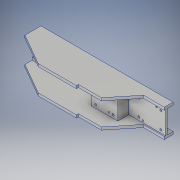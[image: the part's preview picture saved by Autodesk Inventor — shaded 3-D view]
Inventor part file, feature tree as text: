
AUTODESK INVENTOR PART (.ipt)
format: ipt  version: 2017 (Build 210142000, 142)  size: 502,784 bytes
history: native  units: in
note: dims shown in document units (in); Inventor stores cm internally (conversion verified against a paired STEP export)
features: projected_geometry x25, sketch x17, extrude x13, hole x5, reference x4, other x4, chamfer x1
ambient origin geometry x8: Origin, YZ Plane, XZ Plane, XY Plane, X Axis, Y Axis, Z Axis, Center Point
bodies: Solid1 (feature_tree)
feature tree (69):
  extrude  "Extrusion1"  Depth=0.8268in
  extrude  "Extrusion2"  Depth=0.2756in
  extrude  "Extrusion3"  Depth=0.0787in
  extrude  "Extrusion4"  Depth=0.1181in
  extrude  "Extrusion5"  Depth=0.0591in
  hole  "Hole1"  [1 undecoded]
  extrude  "Extrusion6"  Depth=0.0591in
  extrude  "Extrusion7"  Depth=0.7874in
  extrude  "Extrusion8"  Depth=0.2953in TaperAngle=0.0deg
  chamfer  "Chamfer1"  Distance=0.2953in
  hole  "Hole2"  [1 undecoded]
  extrude  "Extrusion9"  Depth=0.4921in
  hole  "Hole3"  [1 undecoded]
  extrude  "Extrusion10"  Depth=0.0591in
  extrude  "Extrusion11"  Depth=0.0591in
  hole  "Hole4"  [1 undecoded]
  extrude  "Extrusion12"  Depth=0.3543in
  hole  "Hole5"  [1 undecoded]
  extrude  "Extrusion13"  Depth=0.2362in
  sketch  "Sketch1"  dims[d0=0.8268in d1=6.4567in]
  sketch  "Sketch2"  dims[d2=1.1417in d3=0.0in d4=0.2756in]
  projected_geometry  "Projected Loop1"
  sketch  "Sketch3"  dims[d5=0.0394in d6=0.0787in]
  sketch  "Sketch4"  dims[d7=0.5906in d8=0.0in d9=0.1181in d10=0.3543in]
  projected_geometry  "Projected Loop2"
  projected_geometry  "Projected Loop3"
  projected_geometry  "Projected Loop4"
  projected_geometry  "Projected Loop5"
  sketch  "Sketch5"  dims[d11=0.1181in d12=0.0591in]
  projected_geometry  "Projected Loop6"
  projected_geometry  "Projected Loop7"
  projected_geometry  "Projected Loop8"
  projected_geometry  "Projected Loop9"
  projected_geometry  "Projected Loop10"
  sketch  "Sketch7"  dims[d13=0.0591in d14=0.0591in]
  projected_geometry  "Projected Loop11"
  sketch  "Sketch8"  dims[d15=0.0591in d16=0.0591in]
  sketch  "Sketch9"  dims[d17=0.0591in d18=0.7874in]
  projected_geometry  "Projected Loop13"
  sketch  "Sketch10"  dims[d19=2.0276in d20=0.2953in d21=0.0in]
  projected_geometry  "Projected Loop14"
  projected_geometry  "Projected Loop15"
  sketch  "Sketch11"  dims[d22=0.2559in]
  projected_geometry  "Projected Loop16"
  sketch  "Sketch12"  dims[d23=0.2953in]
  projected_geometry  "Projected Loop17"
  sketch  "Sketch13"  dims[d24=0.4331in]
  projected_geometry  "Projected Loop18"
  projected_geometry  "Projected Loop19"
  sketch  "Sketch14"  dims[d25=0.9449in]
  projected_geometry  "Projected Loop20"
  projected_geometry  "Projected Loop21"
  sketch  "Sketch15"  dims[d26=0.0787in]
  reference  "Reference1"
  reference  "Reference2"
  sketch  "Sketch16"  dims[d27=0.0787in]
  projected_geometry  "Projected Loop22"
  sketch  "Sketch17"  dims[d28=0.8705in d29=0.2953in d30=0.0in]
  reference  "Reference3"
  reference  "Reference4"
  sketch  "Sketch18"  dims[d31=0.1772in d32=0.0in d33=0.1378in d36=0.4921in d37=0.5118in d39=0.063in d40=0.2362in d41=0.1575in d42=0.0787in d43=90.0deg d44=0.315in d45=0.8108in d46=0.0591in d47=0.0591in d48=0.1378in d49=0.3543in d50=0.3937in d51=0.3543in d52=0.2362in d53=0.0551in d54=0.0in d55=0.1378in d56=0.1378in d57=0.6496in d58=0.0622in d59=0.0in d60=0.0591in d61=0.0591in d62=0.0in d63=0.0591in d64=0.0787in d65=45.0deg d66=0.063in d67=0.2362in d68=0.1575in d69=0.0787in d70=90.0deg d71=0.315in d72=0.8108in d73=0.1772in d74=0.0315in d75=0.0in d77=0.6496in d78=0.4921in d79=0.063in d80=0.2362in d81=0.1575in d82=0.0787in d83=90.0deg d84=0.315in d85=0.8108in d86=0.4331in d87=0.2598in d88=0.2756in d89=0.0394in d90=0.0in d91=4.2126in d92=1.378in d93=0.1378in d94=0.1969in d95=1.9291in d96=0.0394in d97=0.0in d98=0.0433in d99=0.2362in d100=0.1575in d101=0.0787in d102=90.0deg d103=0.315in d104=0.8108in d105=0.6339in d106=0.0591in d107=0.315in d108=0.0in d109=0.0433in d110=0.2362in d111=0.1575in d112=0.0787in d113=90.0deg d114=0.315in d115=0.8108in d116=0.1024in d117=0.2047in d118=0.2598in d119=0.8864in d120=0.4724in d121=0.3937in d122=0.0in]
  projected_geometry  "Projected Loop23"
  projected_geometry  "Projected Loop24"
  projected_geometry  "Projected Loop25"
  projected_geometry  "Projected Loop26"
  other  "<userpath>\Dropbox\Work\HeadSLAM\xtion_internal.iam"
  other  "xtion_internal.iam"
  other  "xtion_ir_cam:1"
  other  "xtion_rgb_cam:1"
note: 5 required parameter values undecoded (feature->parameter linkage not recoverable at this tier; creation-order binding heuristic only, values carry confidence <= 0.55)
